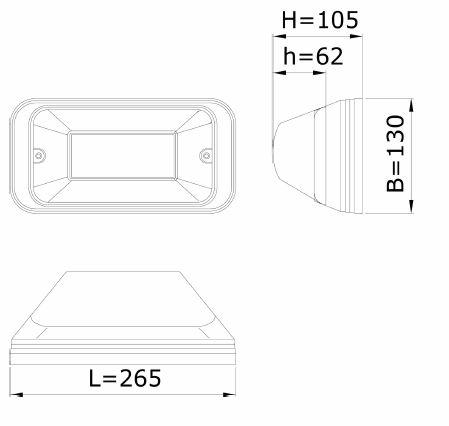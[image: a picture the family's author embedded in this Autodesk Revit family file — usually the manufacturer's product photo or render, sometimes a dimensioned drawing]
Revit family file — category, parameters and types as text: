
# Revit family: Lightronics_LightingFixture_WallAndCeiling_TPK1
name_source: partatom
category: Lighting Fixtures
revit_build: Autodesk Revit 2016 (Build: 20160314_0715(x64)
units: mm (PartAtom-declared; Revit-internal decimal feet)

## family parameters
Cut with Voids When Loaded = No
Host = Face
Light Source = Yes
OmniClass Number = 23.80.70.00
OmniClass Title = Lighting
Part Type = Normal
Room Calculation Point = No
Round Connector Dimension = Use Diameter
Shared = No

## types (1)
- TPK
    Apparent Load = 0 VA
    Assembly Code = D5020200
    AssetType = Fixed
    BIMObjectName = Lightronics_LightingFixture_WallAndCeiling_TPK
    ClassificationName = Uniclass 2015
    ClassificationValue = Pr_70_70_48_85
    Color = Housing: polycarbonate in white RAL 9010, black RAL 9005 or anthracite RAL 7016. Cover: polycarbonate lens, clear prismatic, opal or frosted
    Color Filter = 16777215
    Default Elevation = 1219 mm
    Depth = 130 mm  [stored 0.426509 ft]
    Description = The TPK is a functional and beautifully designed surface-mounted luminaire. The beam can be very easily aimed. The luminaire can be used for both emergency and continuous lighting and is assembly- and maintenance-friendly. The basic unit is identical to that of the TPS luminaire, allowing for the easy exchange of spare parts between both products.
    Dimming Lamp Color Temperature Shift = <None>
    DocumentationLiterature = https://specifi.bimstore.co.uk
    DurationUnit = 20 Years
    Emit from Line Length = 200 mm  [stored 0.656168 ft]
    ExpectedLife = 0
    Height = 103 mm  [stored 0.337927 ft]
    IfcExportAs = IfcLightFixtureTypeEnum.POINTSOURCE
    IfcExportType = IfcLightFixture
    Keynote = V90/510
    Length = 265 mm  [stored 0.869423 ft]
    Manufacturer = Lightronics
    ManufacturerName = Lightronics
    Material = Impact proof polycarbonate
    Model = TPK
    ModelNumber = TPK
    ModelReference = IP 65
    NBSDescription = Surface luminaires
    NBSObjectName = Lightronics -  General purpose luminaires
    NBSReference = 90-60-50/405
    NominalDepth = 130 mm  [stored 0.426509 ft]
    NominalHeight = 103 mm  [stored 0.337927 ft]
    NominalLength = 265 mm  [stored 0.869423 ft]
    NumberOfPoles = 1
    Photometric Web File = generic
    ProductionYear = 2018
    Shape = Rectangular
    Size = 130x103x265
    Tilt Angle = 90.00°
    Type Comments = Wall and ceiling lighting – Impactproof. For directed lighting
    TypeName = TPK
    URL = https://www.lightronics.nl
    Voltage = 230 V
    WarrantyDurationParts = 5
    WarrantyDurationUnit = Years
    _BSBibleVersion = 15
    _BimSpecGuid = 0
    _CurrentRevision = 1
    _DistributedBy = www.bimstore.co.uk

note: [stored X ft] marks values corroborated as IEEE doubles in the binary element streams (Revit-internal decimal feet)

## geometry (parser evidence)
native form markers: Sweep x5
no freeform markers — native parametric forms only
